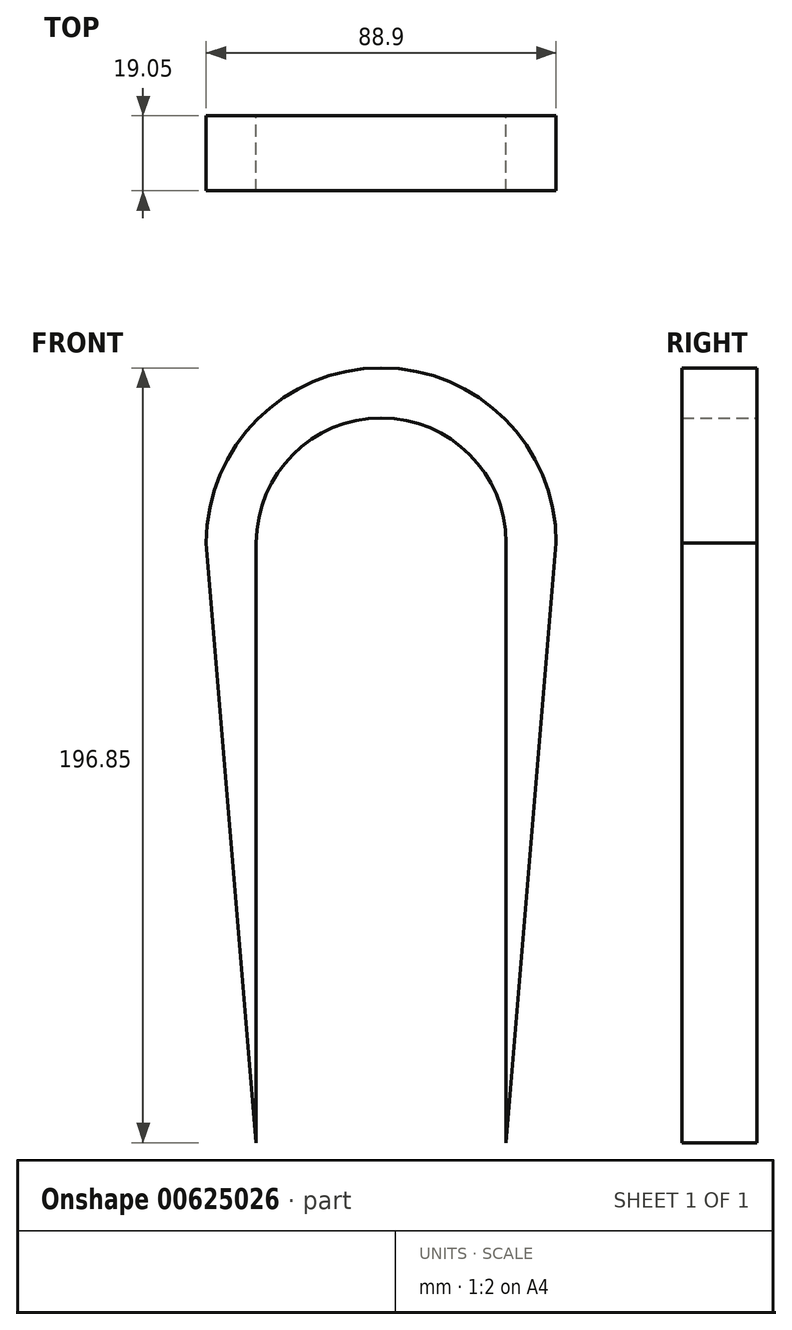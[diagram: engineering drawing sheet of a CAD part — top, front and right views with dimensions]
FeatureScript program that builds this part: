
annotation { "Feature Type Name" : "Feature", "Feature Type Description" : "" }
export const myFeature = defineFeature(function(context is Context, id is Id, definition is map)
    precondition{}
    {
        {
            var Q0;
            Q0=qCreatedBy(makeId("Front.planeOp"),FACE);
            var sketch = newSketch(context, id + "F0", { "sketchPlane" : qUnion([Q0])});
            skArc(sketch, "E0", {"start": v(30.63, 0) * mm, "mid": v(-1.12, 31.75) * mm, "end": v(-32.87, 0) * mm});
            skArc(sketch, "E1", {"start": v(43.33, 0) * mm, "mid": v(-1.12, 44.45) * mm, "end": v(-45.57, 0) * mm});
            skLineSegment(sketch, "E2", {"start": v(-32.87, 0) * mm, "end": v(-32.87, -152.4) * mm});
            skLineSegment(sketch, "E3", {"start": v(-32.87, -152.4) * mm, "end": v(-45.57, 0) * mm});
            skLineSegment(sketch, "E4", {"start": v(30.63, 0) * mm, "end": v(30.63, -152.4) * mm});
            skLineSegment(sketch, "E5", {"start": v(30.63, -152.4) * mm, "end": v(43.33, 0) * mm});
            skSolve(sketch);
        }
        {
            var Q0;
            Q0=makeQuery(id+"F0.imprint","IMPRINT",FACE,{"disambiguationData":[TD([[makeQuery(id+"F0.imprint","IMPRINT",EDGE,{"derivedFrom":sQuery(id+"F0.wireOp",EDGE,"E0")}),-1.0]])]});
            extrude(context, id + "F1", {"entities" : qUnion([Q0]), "depth" : 19.05 * mm, "offsetDistance" : 25.4 * mm});
        }
    });
